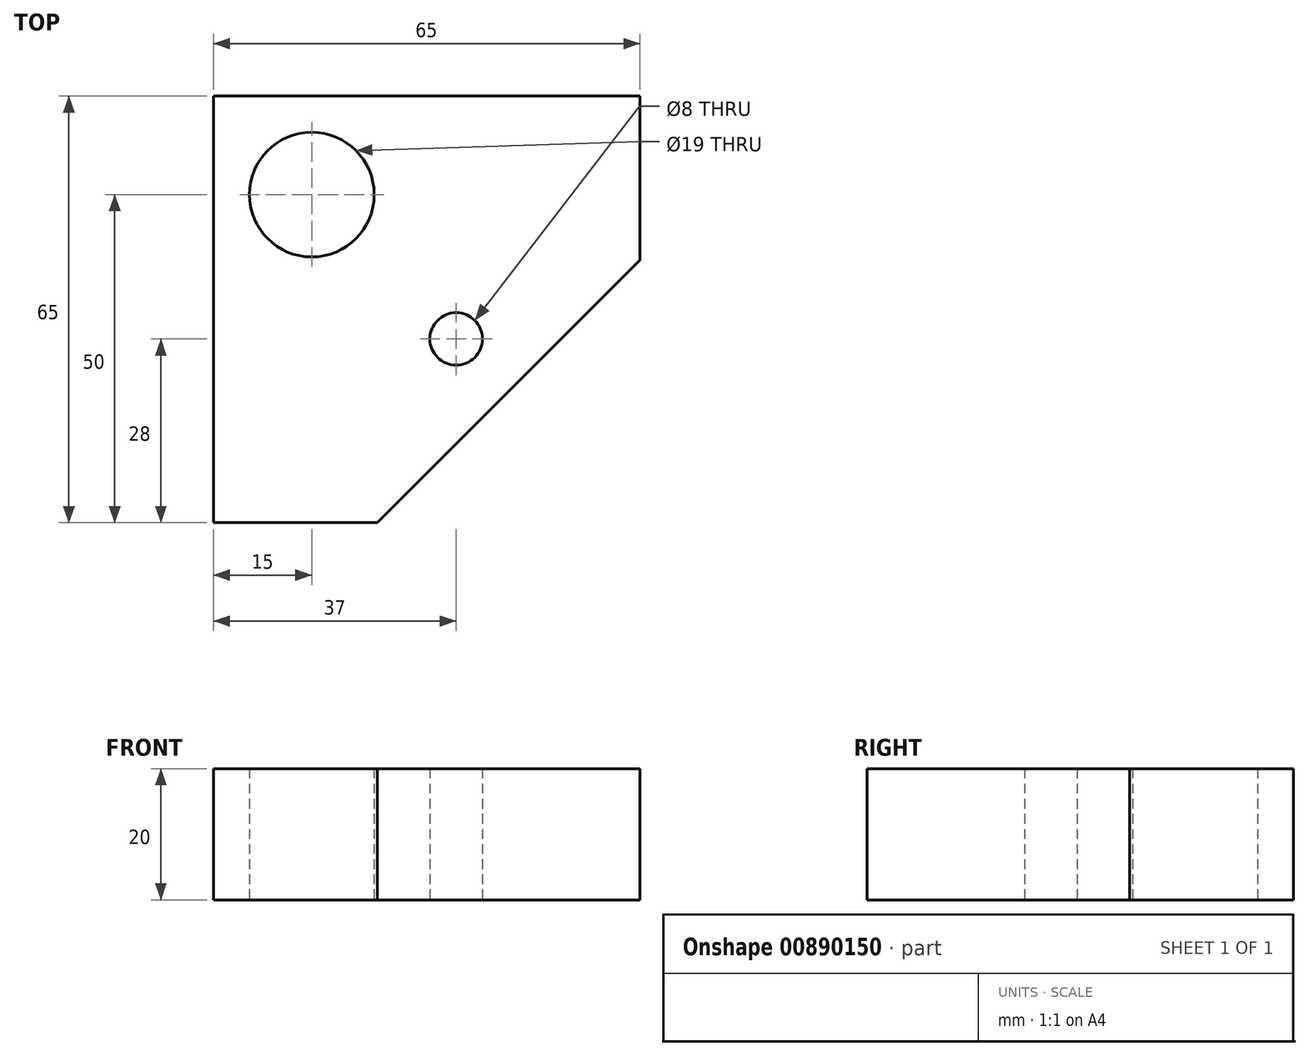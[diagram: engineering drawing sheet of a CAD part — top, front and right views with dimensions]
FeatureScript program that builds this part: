
annotation { "Feature Type Name" : "Feature", "Feature Type Description" : "" }
export const myFeature = defineFeature(function(context is Context, id is Id, definition is map)
    precondition{}
    {
        {
            var Q0;
            Q0=qCreatedBy(makeId("Top.planeOp"),FACE);
            var sketch = newSketch(context, id + "F0", { "sketchPlane" : qUnion([Q0])});
            skCircle(sketch, "E0", {"center": v(15, -15) * mm, "radius": 9.5 * mm});
            skLineSegment(sketch, "E1", {"start": v(25, -65) * mm, "end": v(0, -65) * mm});
            skLineSegment(sketch, "E2", {"start": v(65, -25) * mm, "end": v(65, 0) * mm});
            skLineSegment(sketch, "E3", {"start": v(25, -65) * mm, "end": v(65, -25) * mm});
            skLineSegment(sketch, "E4", {"start": v(0, 0) * mm, "end": v(0, -65) * mm});
            skLineSegment(sketch, "E5", {"start": v(0, 0) * mm, "end": v(65, 0) * mm});
            skLineSegment(sketch, "E6", {"start": v(0, 0) * mm, "end": v(45, -45) * mm});
            skCircle(sketch, "E7", {"center": v(37, -37) * mm, "radius": 4 * mm});
            skSolve(sketch);
        }
        {
            var Q0;
            Q0=qSketchRegion(id+"F0",true);
            extrude(context, id + "F1", {"entities" : qUnion([Q0]), "depth" : 20 * mm, "offsetDistance" : 25 * mm});
        }
    });
